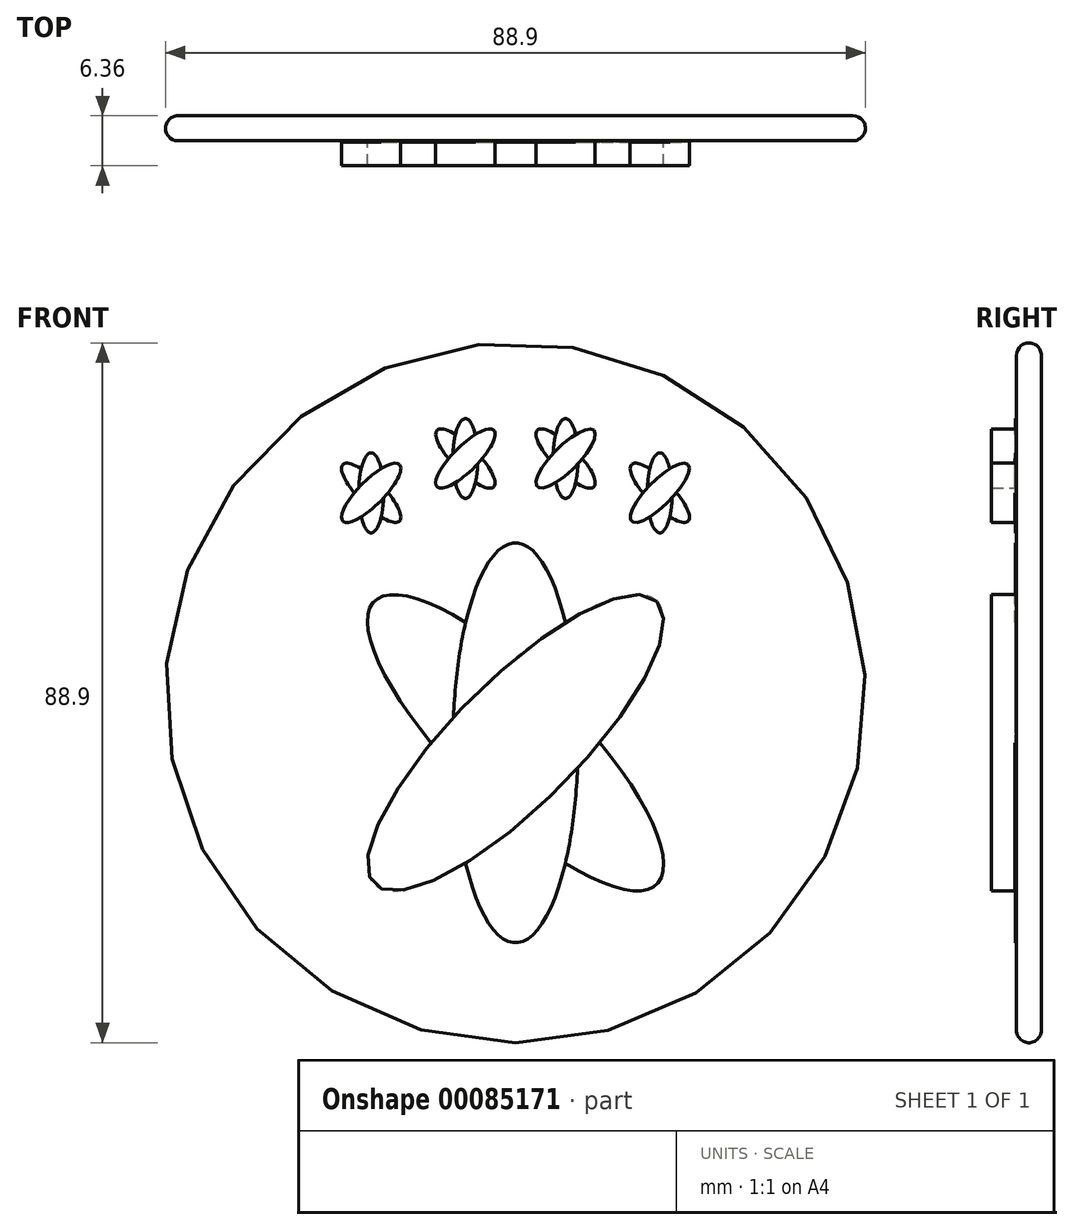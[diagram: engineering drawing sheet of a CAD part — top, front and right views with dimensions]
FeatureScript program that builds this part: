
annotation { "Feature Type Name" : "Feature", "Feature Type Description" : "" }
export const myFeature = defineFeature(function(context is Context, id is Id, definition is map)
    precondition{}
    {
        {
            var Q0;
            Q0=qCreatedBy(makeId("Front.planeOp"),FACE);
            var sketch = newSketch(context, id + "F0", { "sketchPlane" : qUnion([Q0])});
            skEllipse(sketch, "E0", {"center": v(0, 0) * mm, "majorRadius": 25.4 * mm, "minorRadius": 7.94 * mm, "majorAxis": v(0, 1)});
            skEllipse(sketch, "E1", {"center": v(0, 0) * mm, "majorRadius": 25.4 * mm, "minorRadius": 7.94 * mm, "majorAxis": v(0.7, 0.7)});
            skLineSegment(sketch, "E2", {"start": v(0, 0) * mm, "end": v(17.96, 17.96) * mm, "construction": true});
            skEllipse(sketch, "E3.MirrorC", {"center": v(0, 0) * mm, "majorRadius": 25.4 * mm, "minorRadius": 7.94 * mm, "majorAxis": v(-0.7, 0.7)});
            skLineSegment(sketch, "E4", {"start": v(0, 0) * mm, "end": v(-18.33, 31.75) * mm, "construction": true});
            skEllipse(sketch, "E5", {"center": v(-18.33, 31.75) * mm, "majorRadius": 5.08 * mm, "minorRadius": 1.59 * mm, "majorAxis": v(0, 1)});
            skEllipse(sketch, "E6", {"center": v(-18.33, 31.75) * mm, "majorRadius": 5.08 * mm, "minorRadius": 1.59 * mm, "majorAxis": v(0.7, 0.7)});
            skLineSegment(sketch, "E7", {"start": v(-18.33, 31.75) * mm, "end": v(-14.74, 35.34) * mm, "construction": true});
            skLineSegment(sketch, "E8", {"start": v(-18.33, 31.75) * mm, "end": v(-18.33, 36.83) * mm, "construction": true});
            skEllipse(sketch, "E9.MirrorC", {"center": v(-18.33, 31.75) * mm, "majorRadius": 5.08 * mm, "minorRadius": 1.59 * mm, "majorAxis": v(-0.7, 0.7)});
            skEllipse(sketch, "E10.MirrorC", {"center": v(18.33, 31.75) * mm, "majorRadius": 5.08 * mm, "minorRadius": 1.59 * mm, "majorAxis": v(0.7, 0.7)});
            skLineSegment(sketch, "E11.MirrorCS", {"start": v(18.33, 31.75) * mm, "end": v(18.33, 36.83) * mm, "construction": true});
            skLineSegment(sketch, "E12.MirrorCS", {"start": v(18.33, 31.75) * mm, "end": v(14.74, 35.34) * mm, "construction": true});
            skEllipse(sketch, "E13.MirrorC", {"center": v(18.33, 31.75) * mm, "majorRadius": 5.08 * mm, "minorRadius": 1.59 * mm, "majorAxis": v(-0.7, 0.7)});
            skEllipse(sketch, "E14.MirrorC", {"center": v(18.33, 31.75) * mm, "majorRadius": 5.08 * mm, "minorRadius": 1.59 * mm, "majorAxis": v(0, 1)});
            skCircle(sketch, "E15", {"center": v(0, 0) * mm, "radius": 36.66 * mm, "construction": true});
            skPoint(sketch, "E16.endSnap0", {"position": v(-5.61, 5.61) * mm});
            skLineSegment(sketch, "E17", {"start": v(0, 0) * mm, "end": v(-6.37, 36.1) * mm, "construction": true});
            skEllipse(sketch, "E18", {"center": v(-6.37, 36.1) * mm, "majorRadius": 5.08 * mm, "minorRadius": 1.59 * mm, "majorAxis": v(0, 1)});
            skEllipse(sketch, "E19", {"center": v(-6.37, 36.1) * mm, "majorRadius": 5.08 * mm, "minorRadius": 1.59 * mm, "majorAxis": v(0.7, 0.7)});
            skLineSegment(sketch, "E20", {"start": v(-6.37, 36.1) * mm, "end": v(-6.37, 41.18) * mm, "construction": true});
            skLineSegment(sketch, "E21", {"start": v(-6.37, 36.1) * mm, "end": v(-2.77, 39.7) * mm, "construction": true});
            skEllipse(sketch, "E22.MirrorC", {"center": v(-6.37, 36.1) * mm, "majorRadius": 5.08 * mm, "minorRadius": 1.59 * mm, "majorAxis": v(-0.7, 0.7)});
            skLineSegment(sketch, "E23.MirrorCS", {"start": v(6.37, 36.1) * mm, "end": v(6.37, 41.18) * mm, "construction": true});
            skLineSegment(sketch, "E24.MirrorCS", {"start": v(6.37, 36.1) * mm, "end": v(2.77, 39.7) * mm, "construction": true});
            skEllipse(sketch, "E25.MirrorC", {"center": v(6.37, 36.1) * mm, "majorRadius": 5.08 * mm, "minorRadius": 1.59 * mm, "majorAxis": v(0, 1)});
            skEllipse(sketch, "E26.MirrorC", {"center": v(6.37, 36.1) * mm, "majorRadius": 5.08 * mm, "minorRadius": 1.59 * mm, "majorAxis": v(0.7, 0.7)});
            skEllipse(sketch, "E27.MirrorC", {"center": v(6.37, 36.1) * mm, "majorRadius": 5.08 * mm, "minorRadius": 1.59 * mm, "majorAxis": v(-0.7, 0.7)});
            skSolve(sketch);
        }
        {
            var Q0;
            Q0=qCreatedBy(makeId("Front.planeOp"),FACE);
            var sketch = newSketch(context, id + "F5", { "sketchPlane" : qUnion([Q0])});
            skCircle(sketch, "E28", {"center": v(0, 6.35) * mm, "radius": 44.45 * mm});
            skSolve(sketch);
        }
        {
            var Q0;
            Q0 = qSketchRegion(id + "F5", true);
            extrude(context, id + "F6", {"entities" : qUnion([Q0]), "oppositeDirection" : true, "depth" : 3.17 * mm});
        }
        {
            var Q0;
            {var subQ0=sQuery(id+"F0.wireOp",EDGE,"E1");var subQ1=sQuery(id+"F0.wireOp",EDGE,"E0");var subQ2=makeQuery(id+"F0.imprint","INTERSECT",VERTEX,{"disambiguationData":[OD(1.0)],"derivedFrom":[subQ1,subQ0]});Q0=makeQuery(id+"F0.imprint","IMPRINT",FACE,{"disambiguationData":[TD([[makeQuery(id+"F0.imprint","IMPRINT",EDGE,{"disambiguationData":[TD([[subQ2,1.0]])],"derivedFrom":subQ1}),-1.0]])]});}
            var Q1;
            {var subQ0=sQuery(id+"F0.wireOp",EDGE,"E1");var subQ1=sQuery(id+"F0.wireOp",EDGE,"E0");var subQ2=makeQuery(id+"F0.imprint","INTERSECT",VERTEX,{"disambiguationData":[OD(1.0)],"derivedFrom":[subQ1,subQ0]});Q1=makeQuery(id+"F0.imprint","IMPRINT",FACE,{"disambiguationData":[TD([[makeQuery(id+"F0.imprint","IMPRINT",EDGE,{"disambiguationData":[TD([[subQ2,1.0]])],"derivedFrom":subQ1}),1.0]])]});}
            var Q2;
            {var subQ0=sQuery(id+"F0.wireOp",EDGE,"E1");var subQ1=sQuery(id+"F0.wireOp",EDGE,"E0");var subQ2=makeQuery(id+"F0.imprint","INTERSECT",VERTEX,{"disambiguationData":[OD(3.0)],"derivedFrom":[subQ1,subQ0]});Q2=makeQuery(id+"F0.imprint","IMPRINT",FACE,{"disambiguationData":[TD([[makeQuery(id+"F0.imprint","IMPRINT",EDGE,{"disambiguationData":[TD([[subQ2,-1.0]])],"derivedFrom":subQ1}),-1.0]])]});}
            var Q3;
            {var subQ0=sQuery(id+"F0.wireOp",EDGE,"E1");var subQ1=sQuery(id+"F0.wireOp",EDGE,"E0");var subQ6=makeQuery(id+"F0.imprint","INTERSECT",VERTEX,{"disambiguationData":[OD(2.0)],"derivedFrom":[subQ1,subQ0]});Q3=makeQuery(id+"F0.imprint","IMPRINT",FACE,{"disambiguationData":[TD([[makeQuery(id+"F0.imprint","IMPRINT",EDGE,{"disambiguationData":[TD([[subQ6,-1.0]])],"derivedFrom":subQ1}),1.0]])]});}
            var Q4;
            {var subQ0=sQuery(id+"F0.wireOp",EDGE,"E1");var subQ1=sQuery(id+"F0.wireOp",EDGE,"E0");var subQ2=makeQuery(id+"F0.imprint","INTERSECT",VERTEX,{"disambiguationData":[OD(2.0)],"derivedFrom":[subQ1,subQ0]});Q4=makeQuery(id+"F0.imprint","IMPRINT",FACE,{"disambiguationData":[TD([[makeQuery(id+"F0.imprint","IMPRINT",EDGE,{"disambiguationData":[TD([[subQ2,-1.0]])],"derivedFrom":subQ1}),-1.0]])]});}
            var Q5;
            {var subQ0=sQuery(id+"F0.wireOp",EDGE,"E1");var subQ1=sQuery(id+"F0.wireOp",EDGE,"E0");var subQ2=makeQuery(id+"F0.imprint","INTERSECT",VERTEX,{"disambiguationData":[OD(0.0)],"derivedFrom":[subQ1,subQ0]});Q5=makeQuery(id+"F0.imprint","IMPRINT",FACE,{"disambiguationData":[TD([[makeQuery(id+"F0.imprint","IMPRINT",EDGE,{"disambiguationData":[TD([[subQ2,1.0]])],"derivedFrom":subQ1}),1.0]])]});}
            var Q6;
            {var subQ0=sQuery(id+"F0.wireOp",EDGE,"E1");var subQ1=sQuery(id+"F0.wireOp",EDGE,"E0");var subQ2=makeQuery(id+"F0.imprint","INTERSECT",VERTEX,{"disambiguationData":[OD(0.0)],"derivedFrom":[subQ1,subQ0]});Q6=makeQuery(id+"F0.imprint","IMPRINT",FACE,{"disambiguationData":[TD([[makeQuery(id+"F0.imprint","IMPRINT",EDGE,{"disambiguationData":[TD([[subQ2,1.0]])],"derivedFrom":subQ1}),-1.0]])]});}
            var Q7;
            {var subQ0=sQuery(id+"F0.wireOp",EDGE,"E6");var subQ1=sQuery(id+"F0.wireOp",EDGE,"E5");var subQ2=makeQuery(id+"F0.imprint","INTERSECT",VERTEX,{"disambiguationData":[OD(1.0)],"derivedFrom":[subQ1,subQ0]});Q7=makeQuery(id+"F0.imprint","IMPRINT",FACE,{"disambiguationData":[TD([[makeQuery(id+"F0.imprint","IMPRINT",EDGE,{"disambiguationData":[TD([[subQ2,1.0]])],"derivedFrom":subQ1}),-1.0]])]});}
            var Q8;
            {var subQ0=sQuery(id+"F0.wireOp",EDGE,"E6");var subQ1=sQuery(id+"F0.wireOp",EDGE,"E5");var subQ2=makeQuery(id+"F0.imprint","INTERSECT",VERTEX,{"disambiguationData":[OD(1.0)],"derivedFrom":[subQ1,subQ0]});Q8=makeQuery(id+"F0.imprint","IMPRINT",FACE,{"disambiguationData":[TD([[makeQuery(id+"F0.imprint","IMPRINT",EDGE,{"disambiguationData":[TD([[subQ2,1.0]])],"derivedFrom":subQ1}),1.0]])]});}
            var Q9;
            {var subQ0=sQuery(id+"F0.wireOp",EDGE,"E6");var subQ1=sQuery(id+"F0.wireOp",EDGE,"E5");var subQ2=makeQuery(id+"F0.imprint","INTERSECT",VERTEX,{"disambiguationData":[OD(3.0)],"derivedFrom":[subQ1,subQ0]});Q9=makeQuery(id+"F0.imprint","IMPRINT",FACE,{"disambiguationData":[TD([[makeQuery(id+"F0.imprint","IMPRINT",EDGE,{"disambiguationData":[TD([[subQ2,-1.0]])],"derivedFrom":subQ1}),-1.0]])]});}
            var Q10;
            {var subQ0=sQuery(id+"F0.wireOp",EDGE,"E6");var subQ1=sQuery(id+"F0.wireOp",EDGE,"E5");var subQ5=makeQuery(id+"F0.imprint","INTERSECT",VERTEX,{"disambiguationData":[OD(2.0)],"derivedFrom":[subQ1,subQ0]});Q10=makeQuery(id+"F0.imprint","IMPRINT",FACE,{"disambiguationData":[TD([[makeQuery(id+"F0.imprint","IMPRINT",EDGE,{"disambiguationData":[TD([[subQ5,-1.0]])],"derivedFrom":subQ1}),1.0]])]});}
            var Q11;
            {var subQ0=sQuery(id+"F0.wireOp",EDGE,"E6");var subQ1=sQuery(id+"F0.wireOp",EDGE,"E5");var subQ2=makeQuery(id+"F0.imprint","INTERSECT",VERTEX,{"disambiguationData":[OD(2.0)],"derivedFrom":[subQ1,subQ0]});Q11=makeQuery(id+"F0.imprint","IMPRINT",FACE,{"disambiguationData":[TD([[makeQuery(id+"F0.imprint","IMPRINT",EDGE,{"disambiguationData":[TD([[subQ2,-1.0]])],"derivedFrom":subQ1}),-1.0]])]});}
            var Q12;
            {var subQ0=sQuery(id+"F0.wireOp",EDGE,"E6");var subQ1=sQuery(id+"F0.wireOp",EDGE,"E5");var subQ2=makeQuery(id+"F0.imprint","INTERSECT",VERTEX,{"disambiguationData":[OD(0.0)],"derivedFrom":[subQ1,subQ0]});Q12=makeQuery(id+"F0.imprint","IMPRINT",FACE,{"disambiguationData":[TD([[makeQuery(id+"F0.imprint","IMPRINT",EDGE,{"disambiguationData":[TD([[subQ2,1.0]])],"derivedFrom":subQ1}),1.0]])]});}
            var Q13;
            {var subQ0=sQuery(id+"F0.wireOp",EDGE,"E6");var subQ1=sQuery(id+"F0.wireOp",EDGE,"E5");var subQ2=makeQuery(id+"F0.imprint","INTERSECT",VERTEX,{"disambiguationData":[OD(0.0)],"derivedFrom":[subQ1,subQ0]});Q13=makeQuery(id+"F0.imprint","IMPRINT",FACE,{"disambiguationData":[TD([[makeQuery(id+"F0.imprint","IMPRINT",EDGE,{"disambiguationData":[TD([[subQ2,1.0]])],"derivedFrom":subQ1}),-1.0]])]});}
            var Q14;
            {var subQ0=sQuery(id+"F0.wireOp",EDGE,"E19");var subQ1=sQuery(id+"F0.wireOp",EDGE,"E18");var subQ2=makeQuery(id+"F0.imprint","INTERSECT",VERTEX,{"disambiguationData":[OD(0.0)],"derivedFrom":[subQ1,subQ0]});Q14=makeQuery(id+"F0.imprint","IMPRINT",FACE,{"disambiguationData":[TD([[makeQuery(id+"F0.imprint","IMPRINT",EDGE,{"disambiguationData":[TD([[subQ2,1.0]])],"derivedFrom":subQ1}),-1.0]])]});}
            var Q15;
            {var subQ0=sQuery(id+"F0.wireOp",EDGE,"E19");var subQ1=sQuery(id+"F0.wireOp",EDGE,"E18");var subQ2=makeQuery(id+"F0.imprint","INTERSECT",VERTEX,{"disambiguationData":[OD(0.0)],"derivedFrom":[subQ1,subQ0]});Q15=makeQuery(id+"F0.imprint","IMPRINT",FACE,{"disambiguationData":[TD([[makeQuery(id+"F0.imprint","IMPRINT",EDGE,{"disambiguationData":[TD([[subQ2,1.0]])],"derivedFrom":subQ1}),1.0]])]});}
            var Q16;
            {var subQ0=sQuery(id+"F0.wireOp",EDGE,"E19");var subQ1=sQuery(id+"F0.wireOp",EDGE,"E18");var subQ2=makeQuery(id+"F0.imprint","INTERSECT",VERTEX,{"disambiguationData":[OD(2.0)],"derivedFrom":[subQ1,subQ0]});Q16=makeQuery(id+"F0.imprint","IMPRINT",FACE,{"disambiguationData":[TD([[makeQuery(id+"F0.imprint","IMPRINT",EDGE,{"disambiguationData":[TD([[subQ2,-1.0]])],"derivedFrom":subQ1}),-1.0]])]});}
            var Q17;
            {var subQ0=sQuery(id+"F0.wireOp",EDGE,"E19");var subQ1=sQuery(id+"F0.wireOp",EDGE,"E18");var subQ5=makeQuery(id+"F0.imprint","INTERSECT",VERTEX,{"disambiguationData":[OD(2.0)],"derivedFrom":[subQ1,subQ0]});Q17=makeQuery(id+"F0.imprint","IMPRINT",FACE,{"disambiguationData":[TD([[makeQuery(id+"F0.imprint","IMPRINT",EDGE,{"disambiguationData":[TD([[subQ5,-1.0]])],"derivedFrom":subQ1}),1.0]])]});}
            var Q18;
            {var subQ0=sQuery(id+"F0.wireOp",EDGE,"E19");var subQ1=sQuery(id+"F0.wireOp",EDGE,"E18");var subQ2=makeQuery(id+"F0.imprint","INTERSECT",VERTEX,{"disambiguationData":[OD(3.0)],"derivedFrom":[subQ1,subQ0]});Q18=makeQuery(id+"F0.imprint","IMPRINT",FACE,{"disambiguationData":[TD([[makeQuery(id+"F0.imprint","IMPRINT",EDGE,{"disambiguationData":[TD([[subQ2,-1.0]])],"derivedFrom":subQ1}),-1.0]])]});}
            var Q19;
            {var subQ0=sQuery(id+"F0.wireOp",EDGE,"E19");var subQ1=sQuery(id+"F0.wireOp",EDGE,"E18");var subQ2=makeQuery(id+"F0.imprint","INTERSECT",VERTEX,{"disambiguationData":[OD(1.0)],"derivedFrom":[subQ1,subQ0]});Q19=makeQuery(id+"F0.imprint","IMPRINT",FACE,{"disambiguationData":[TD([[makeQuery(id+"F0.imprint","IMPRINT",EDGE,{"disambiguationData":[TD([[subQ2,1.0]])],"derivedFrom":subQ1}),-1.0]])]});}
            var Q20;
            {var subQ0=sQuery(id+"F0.wireOp",EDGE,"E19");var subQ1=sQuery(id+"F0.wireOp",EDGE,"E18");var subQ2=makeQuery(id+"F0.imprint","INTERSECT",VERTEX,{"disambiguationData":[OD(1.0)],"derivedFrom":[subQ1,subQ0]});Q20=makeQuery(id+"F0.imprint","IMPRINT",FACE,{"disambiguationData":[TD([[makeQuery(id+"F0.imprint","IMPRINT",EDGE,{"disambiguationData":[TD([[subQ2,1.0]])],"derivedFrom":subQ1}),1.0]])]});}
            var Q21;
            {var subQ0=sQuery(id+"F0.wireOp",EDGE,"E26.MirrorC");var subQ1=sQuery(id+"F0.wireOp",EDGE,"E25.MirrorC");var subQ2=makeQuery(id+"F0.imprint","INTERSECT",VERTEX,{"disambiguationData":[OD(0.0)],"derivedFrom":[subQ1,subQ0]});Q21=makeQuery(id+"F0.imprint","IMPRINT",FACE,{"disambiguationData":[TD([[makeQuery(id+"F0.imprint","IMPRINT",EDGE,{"disambiguationData":[TD([[subQ2,1.0]])],"derivedFrom":subQ1}),-1.0]])]});}
            var Q22;
            {var subQ0=sQuery(id+"F0.wireOp",EDGE,"E26.MirrorC");var subQ1=sQuery(id+"F0.wireOp",EDGE,"E25.MirrorC");var subQ2=makeQuery(id+"F0.imprint","INTERSECT",VERTEX,{"disambiguationData":[OD(0.0)],"derivedFrom":[subQ1,subQ0]});Q22=makeQuery(id+"F0.imprint","IMPRINT",FACE,{"disambiguationData":[TD([[makeQuery(id+"F0.imprint","IMPRINT",EDGE,{"disambiguationData":[TD([[subQ2,1.0]])],"derivedFrom":subQ1}),1.0]])]});}
            var Q23;
            {var subQ0=sQuery(id+"F0.wireOp",EDGE,"E26.MirrorC");var subQ1=sQuery(id+"F0.wireOp",EDGE,"E25.MirrorC");var subQ2=makeQuery(id+"F0.imprint","INTERSECT",VERTEX,{"disambiguationData":[OD(2.0)],"derivedFrom":[subQ1,subQ0]});Q23=makeQuery(id+"F0.imprint","IMPRINT",FACE,{"disambiguationData":[TD([[makeQuery(id+"F0.imprint","IMPRINT",EDGE,{"disambiguationData":[TD([[subQ2,-1.0]])],"derivedFrom":subQ1}),-1.0]])]});}
            var Q24;
            {var subQ0=sQuery(id+"F0.wireOp",EDGE,"E26.MirrorC");var subQ1=sQuery(id+"F0.wireOp",EDGE,"E25.MirrorC");var subQ5=makeQuery(id+"F0.imprint","INTERSECT",VERTEX,{"disambiguationData":[OD(2.0)],"derivedFrom":[subQ1,subQ0]});Q24=makeQuery(id+"F0.imprint","IMPRINT",FACE,{"disambiguationData":[TD([[makeQuery(id+"F0.imprint","IMPRINT",EDGE,{"disambiguationData":[TD([[subQ5,-1.0]])],"derivedFrom":subQ1}),1.0]])]});}
            var Q25;
            {var subQ0=sQuery(id+"F0.wireOp",EDGE,"E26.MirrorC");var subQ1=sQuery(id+"F0.wireOp",EDGE,"E25.MirrorC");var subQ2=makeQuery(id+"F0.imprint","INTERSECT",VERTEX,{"disambiguationData":[OD(3.0)],"derivedFrom":[subQ1,subQ0]});Q25=makeQuery(id+"F0.imprint","IMPRINT",FACE,{"disambiguationData":[TD([[makeQuery(id+"F0.imprint","IMPRINT",EDGE,{"disambiguationData":[TD([[subQ2,-1.0]])],"derivedFrom":subQ1}),-1.0]])]});}
            var Q26;
            {var subQ0=sQuery(id+"F0.wireOp",EDGE,"E26.MirrorC");var subQ1=sQuery(id+"F0.wireOp",EDGE,"E25.MirrorC");var subQ2=makeQuery(id+"F0.imprint","INTERSECT",VERTEX,{"disambiguationData":[OD(1.0)],"derivedFrom":[subQ1,subQ0]});Q26=makeQuery(id+"F0.imprint","IMPRINT",FACE,{"disambiguationData":[TD([[makeQuery(id+"F0.imprint","IMPRINT",EDGE,{"disambiguationData":[TD([[subQ2,1.0]])],"derivedFrom":subQ1}),1.0]])]});}
            var Q27;
            {var subQ0=sQuery(id+"F0.wireOp",EDGE,"E26.MirrorC");var subQ1=sQuery(id+"F0.wireOp",EDGE,"E25.MirrorC");var subQ2=makeQuery(id+"F0.imprint","INTERSECT",VERTEX,{"disambiguationData":[OD(1.0)],"derivedFrom":[subQ1,subQ0]});Q27=makeQuery(id+"F0.imprint","IMPRINT",FACE,{"disambiguationData":[TD([[makeQuery(id+"F0.imprint","IMPRINT",EDGE,{"disambiguationData":[TD([[subQ2,1.0]])],"derivedFrom":subQ1}),-1.0]])]});}
            var Q28;
            {var subQ0=sQuery(id+"F0.wireOp",EDGE,"E13.MirrorC");var subQ1=sQuery(id+"F0.wireOp",EDGE,"E10.MirrorC");var subQ2=makeQuery(id+"F0.imprint","INTERSECT",VERTEX,{"disambiguationData":[OD(0.0)],"derivedFrom":[subQ1,subQ0]});Q28=makeQuery(id+"F0.imprint","IMPRINT",FACE,{"disambiguationData":[TD([[makeQuery(id+"F0.imprint","IMPRINT",EDGE,{"disambiguationData":[TD([[subQ2,-1.0]])],"derivedFrom":subQ1}),1.0]])]});}
            var Q29;
            {var subQ0=sQuery(id+"F0.wireOp",EDGE,"E14.MirrorC");var subQ1=sQuery(id+"F0.wireOp",EDGE,"E10.MirrorC");var subQ2=makeQuery(id+"F0.imprint","INTERSECT",VERTEX,{"disambiguationData":[OD(1.0)],"derivedFrom":[subQ1,subQ0]});Q29=makeQuery(id+"F0.imprint","IMPRINT",FACE,{"disambiguationData":[TD([[makeQuery(id+"F0.imprint","IMPRINT",EDGE,{"disambiguationData":[TD([[subQ2,-1.0]])],"derivedFrom":subQ1}),1.0]])]});}
            var Q30;
            {var subQ0=sQuery(id+"F0.wireOp",EDGE,"E13.MirrorC");var subQ1=sQuery(id+"F0.wireOp",EDGE,"E10.MirrorC");var subQ2=makeQuery(id+"F0.imprint","INTERSECT",VERTEX,{"disambiguationData":[OD(0.0)],"derivedFrom":[subQ1,subQ0]});Q30=makeQuery(id+"F0.imprint","IMPRINT",FACE,{"disambiguationData":[TD([[makeQuery(id+"F0.imprint","IMPRINT",EDGE,{"disambiguationData":[TD([[subQ2,1.0]])],"derivedFrom":subQ1}),1.0]])]});}
            var Q31;
            {var subQ0=sQuery(id+"F0.wireOp",EDGE,"E13.MirrorC");var subQ1=sQuery(id+"F0.wireOp",EDGE,"E10.MirrorC");var subQ2=makeQuery(id+"F0.imprint","INTERSECT",VERTEX,{"disambiguationData":[OD(2.0)],"derivedFrom":[subQ1,subQ0]});Q31=makeQuery(id+"F0.imprint","IMPRINT",FACE,{"disambiguationData":[TD([[makeQuery(id+"F0.imprint","IMPRINT",EDGE,{"disambiguationData":[TD([[subQ2,-1.0]])],"derivedFrom":subQ1}),1.0]])]});}
            var Q32;
            {var subQ0=sQuery(id+"F0.wireOp",EDGE,"E14.MirrorC");var subQ1=sQuery(id+"F0.wireOp",EDGE,"E10.MirrorC");var subQ2=makeQuery(id+"F0.imprint","INTERSECT",VERTEX,{"disambiguationData":[OD(0.0)],"derivedFrom":[subQ1,subQ0]});Q32=makeQuery(id+"F0.imprint","IMPRINT",FACE,{"disambiguationData":[TD([[makeQuery(id+"F0.imprint","IMPRINT",EDGE,{"disambiguationData":[TD([[subQ2,-1.0]])],"derivedFrom":subQ1}),1.0]])]});}
            var Q33;
            {var subQ0=sQuery(id+"F0.wireOp",EDGE,"E13.MirrorC");var subQ1=sQuery(id+"F0.wireOp",EDGE,"E10.MirrorC");var subQ2=makeQuery(id+"F0.imprint","INTERSECT",VERTEX,{"disambiguationData":[OD(1.0)],"derivedFrom":[subQ1,subQ0]});Q33=makeQuery(id+"F0.imprint","IMPRINT",FACE,{"disambiguationData":[TD([[makeQuery(id+"F0.imprint","IMPRINT",EDGE,{"disambiguationData":[TD([[subQ2,1.0]])],"derivedFrom":subQ1}),1.0]])]});}
            var Q34;
            {var subQ0=sQuery(id+"F0.wireOp",EDGE,"E14.MirrorC");var subQ1=sQuery(id+"F0.wireOp",EDGE,"E10.MirrorC");var subQ2=makeQuery(id+"F0.imprint","INTERSECT",VERTEX,{"disambiguationData":[OD(0.0)],"derivedFrom":[subQ1,subQ0]});Q34=makeQuery(id+"F0.imprint","IMPRINT",FACE,{"disambiguationData":[TD([[makeQuery(id+"F0.imprint","IMPRINT",EDGE,{"disambiguationData":[TD([[subQ2,1.0]])],"derivedFrom":subQ1}),1.0]])]});}
            extrude(context, id + "F1", {"entities" : qUnion([Q0, Q1, Q2, Q3, Q4, Q5, Q6, Q7, Q8, Q9, Q10, Q11, Q12, Q13, Q14, Q15, Q16, Q17, Q18, Q19, Q20, Q21, Q22, Q23, Q24, Q25, Q26, Q27, Q28, Q29, Q30, Q31, Q32, Q33, Q34]), "operationType" : NewBodyOperationType.ADD, "depth" : 3.17 * mm});
        }
        {
            var Q0;
            {var subQ0=sQuery(id+"F0.wireOp",EDGE,"E3.MirrorC");var subQ1=sQuery(id+"F0.wireOp",EDGE,"E0");var subQ2=makeQuery(id+"F0.imprint","INTERSECT",VERTEX,{"disambiguationData":[OD(0.0)],"derivedFrom":[subQ1,subQ0]});Q0=makeQuery(id+"F0.imprint","IMPRINT",FACE,{"disambiguationData":[TD([[makeQuery(id+"F0.imprint","IMPRINT",EDGE,{"disambiguationData":[TD([[subQ2,1.0]])],"derivedFrom":subQ1}),1.0]])]});}
            var Q1;
            {var subQ0=sQuery(id+"F0.wireOp",EDGE,"E3.MirrorC");var subQ1=sQuery(id+"F0.wireOp",EDGE,"E0");var subQ2=makeQuery(id+"F0.imprint","INTERSECT",VERTEX,{"disambiguationData":[OD(0.0)],"derivedFrom":[subQ1,subQ0]});Q1=makeQuery(id+"F0.imprint","IMPRINT",FACE,{"disambiguationData":[TD([[makeQuery(id+"F0.imprint","IMPRINT",EDGE,{"disambiguationData":[TD([[subQ2,-1.0]])],"derivedFrom":subQ1}),1.0]])]});}
            var Q2;
            {var subQ0=sQuery(id+"F0.wireOp",EDGE,"E3.MirrorC");var subQ1=sQuery(id+"F0.wireOp",EDGE,"E0");var subQ2=makeQuery(id+"F0.imprint","INTERSECT",VERTEX,{"disambiguationData":[OD(1.0)],"derivedFrom":[subQ1,subQ0]});Q2=makeQuery(id+"F0.imprint","IMPRINT",FACE,{"disambiguationData":[TD([[makeQuery(id+"F0.imprint","IMPRINT",EDGE,{"disambiguationData":[TD([[subQ2,-1.0]])],"derivedFrom":subQ1}),1.0]])]});}
            var Q3;
            {var subQ0=sQuery(id+"F0.wireOp",EDGE,"E1");var subQ1=sQuery(id+"F0.wireOp",EDGE,"E0");var subQ2=makeQuery(id+"F0.imprint","INTERSECT",VERTEX,{"disambiguationData":[OD(0.0)],"derivedFrom":[subQ1,subQ0]});Q3=makeQuery(id+"F0.imprint","IMPRINT",FACE,{"disambiguationData":[TD([[makeQuery(id+"F0.imprint","IMPRINT",EDGE,{"disambiguationData":[TD([[subQ2,-1.0]])],"derivedFrom":subQ1}),1.0]])]});}
            var Q4;
            {var subQ0=sQuery(id+"F0.wireOp",EDGE,"E6");var subQ1=sQuery(id+"F0.wireOp",EDGE,"E5");var subQ2=makeQuery(id+"F0.imprint","INTERSECT",VERTEX,{"disambiguationData":[OD(0.0)],"derivedFrom":[subQ1,subQ0]});Q4=makeQuery(id+"F0.imprint","IMPRINT",FACE,{"disambiguationData":[TD([[makeQuery(id+"F0.imprint","IMPRINT",EDGE,{"disambiguationData":[TD([[subQ2,-1.0]])],"derivedFrom":subQ1}),1.0]])]});}
            var Q5;
            {var subQ0=sQuery(id+"F0.wireOp",EDGE,"E9.MirrorC");var subQ1=sQuery(id+"F0.wireOp",EDGE,"E5");var subQ2=makeQuery(id+"F0.imprint","INTERSECT",VERTEX,{"disambiguationData":[OD(1.0)],"derivedFrom":[subQ1,subQ0]});Q5=makeQuery(id+"F0.imprint","IMPRINT",FACE,{"disambiguationData":[TD([[makeQuery(id+"F0.imprint","IMPRINT",EDGE,{"disambiguationData":[TD([[subQ2,-1.0]])],"derivedFrom":subQ1}),1.0]])]});}
            var Q6;
            {var subQ0=sQuery(id+"F0.wireOp",EDGE,"E9.MirrorC");var subQ1=sQuery(id+"F0.wireOp",EDGE,"E5");var subQ2=makeQuery(id+"F0.imprint","INTERSECT",VERTEX,{"disambiguationData":[OD(0.0)],"derivedFrom":[subQ1,subQ0]});Q6=makeQuery(id+"F0.imprint","IMPRINT",FACE,{"disambiguationData":[TD([[makeQuery(id+"F0.imprint","IMPRINT",EDGE,{"disambiguationData":[TD([[subQ2,-1.0]])],"derivedFrom":subQ1}),1.0]])]});}
            var Q7;
            {var subQ0=sQuery(id+"F0.wireOp",EDGE,"E9.MirrorC");var subQ1=sQuery(id+"F0.wireOp",EDGE,"E5");var subQ2=makeQuery(id+"F0.imprint","INTERSECT",VERTEX,{"disambiguationData":[OD(0.0)],"derivedFrom":[subQ1,subQ0]});Q7=makeQuery(id+"F0.imprint","IMPRINT",FACE,{"disambiguationData":[TD([[makeQuery(id+"F0.imprint","IMPRINT",EDGE,{"disambiguationData":[TD([[subQ2,1.0]])],"derivedFrom":subQ1}),1.0]])]});}
            var Q8;
            {var subQ0=sQuery(id+"F0.wireOp",EDGE,"E22.MirrorC");var subQ1=sQuery(id+"F0.wireOp",EDGE,"E18");var subQ2=makeQuery(id+"F0.imprint","INTERSECT",VERTEX,{"disambiguationData":[OD(0.0)],"derivedFrom":[subQ1,subQ0]});Q8=makeQuery(id+"F0.imprint","IMPRINT",FACE,{"disambiguationData":[TD([[makeQuery(id+"F0.imprint","IMPRINT",EDGE,{"disambiguationData":[TD([[subQ2,-1.0]])],"derivedFrom":subQ1}),1.0]])]});}
            var Q9;
            {var subQ0=sQuery(id+"F0.wireOp",EDGE,"E22.MirrorC");var subQ1=sQuery(id+"F0.wireOp",EDGE,"E18");var subQ2=makeQuery(id+"F0.imprint","INTERSECT",VERTEX,{"disambiguationData":[OD(0.0)],"derivedFrom":[subQ1,subQ0]});Q9=makeQuery(id+"F0.imprint","IMPRINT",FACE,{"disambiguationData":[TD([[makeQuery(id+"F0.imprint","IMPRINT",EDGE,{"disambiguationData":[TD([[subQ2,1.0]])],"derivedFrom":subQ1}),1.0]])]});}
            var Q10;
            {var subQ0=sQuery(id+"F0.wireOp",EDGE,"E22.MirrorC");var subQ1=sQuery(id+"F0.wireOp",EDGE,"E18");var subQ2=makeQuery(id+"F0.imprint","INTERSECT",VERTEX,{"disambiguationData":[OD(1.0)],"derivedFrom":[subQ1,subQ0]});Q10=makeQuery(id+"F0.imprint","IMPRINT",FACE,{"disambiguationData":[TD([[makeQuery(id+"F0.imprint","IMPRINT",EDGE,{"disambiguationData":[TD([[subQ2,-1.0]])],"derivedFrom":subQ1}),1.0]])]});}
            var Q11;
            {var subQ0=sQuery(id+"F0.wireOp",EDGE,"E19");var subQ1=sQuery(id+"F0.wireOp",EDGE,"E18");var subQ2=makeQuery(id+"F0.imprint","INTERSECT",VERTEX,{"disambiguationData":[OD(0.0)],"derivedFrom":[subQ1,subQ0]});Q11=makeQuery(id+"F0.imprint","IMPRINT",FACE,{"disambiguationData":[TD([[makeQuery(id+"F0.imprint","IMPRINT",EDGE,{"disambiguationData":[TD([[subQ2,-1.0]])],"derivedFrom":subQ1}),1.0]])]});}
            var Q12;
            {var subQ0=sQuery(id+"F0.wireOp",EDGE,"E26.MirrorC");var subQ1=sQuery(id+"F0.wireOp",EDGE,"E25.MirrorC");var subQ2=makeQuery(id+"F0.imprint","INTERSECT",VERTEX,{"disambiguationData":[OD(0.0)],"derivedFrom":[subQ1,subQ0]});Q12=makeQuery(id+"F0.imprint","IMPRINT",FACE,{"disambiguationData":[TD([[makeQuery(id+"F0.imprint","IMPRINT",EDGE,{"disambiguationData":[TD([[subQ2,-1.0]])],"derivedFrom":subQ1}),1.0]])]});}
            var Q13;
            {var subQ0=sQuery(id+"F0.wireOp",EDGE,"E27.MirrorC");var subQ1=sQuery(id+"F0.wireOp",EDGE,"E25.MirrorC");var subQ2=makeQuery(id+"F0.imprint","INTERSECT",VERTEX,{"disambiguationData":[OD(1.0)],"derivedFrom":[subQ1,subQ0]});Q13=makeQuery(id+"F0.imprint","IMPRINT",FACE,{"disambiguationData":[TD([[makeQuery(id+"F0.imprint","IMPRINT",EDGE,{"disambiguationData":[TD([[subQ2,-1.0]])],"derivedFrom":subQ1}),1.0]])]});}
            var Q14;
            {var subQ0=sQuery(id+"F0.wireOp",EDGE,"E27.MirrorC");var subQ1=sQuery(id+"F0.wireOp",EDGE,"E25.MirrorC");var subQ2=makeQuery(id+"F0.imprint","INTERSECT",VERTEX,{"disambiguationData":[OD(0.0)],"derivedFrom":[subQ1,subQ0]});Q14=makeQuery(id+"F0.imprint","IMPRINT",FACE,{"disambiguationData":[TD([[makeQuery(id+"F0.imprint","IMPRINT",EDGE,{"disambiguationData":[TD([[subQ2,-1.0]])],"derivedFrom":subQ1}),1.0]])]});}
            var Q15;
            {var subQ0=sQuery(id+"F0.wireOp",EDGE,"E27.MirrorC");var subQ1=sQuery(id+"F0.wireOp",EDGE,"E25.MirrorC");var subQ2=makeQuery(id+"F0.imprint","INTERSECT",VERTEX,{"disambiguationData":[OD(0.0)],"derivedFrom":[subQ1,subQ0]});Q15=makeQuery(id+"F0.imprint","IMPRINT",FACE,{"disambiguationData":[TD([[makeQuery(id+"F0.imprint","IMPRINT",EDGE,{"disambiguationData":[TD([[subQ2,1.0]])],"derivedFrom":subQ1}),1.0]])]});}
            var Q16;
            {var subQ0=sQuery(id+"F0.wireOp",EDGE,"E14.MirrorC");var subQ1=sQuery(id+"F0.wireOp",EDGE,"E10.MirrorC");var subQ2=makeQuery(id+"F0.imprint","INTERSECT",VERTEX,{"disambiguationData":[OD(0.0)],"derivedFrom":[subQ1,subQ0]});Q16=makeQuery(id+"F0.imprint","IMPRINT",FACE,{"disambiguationData":[TD([[makeQuery(id+"F0.imprint","IMPRINT",EDGE,{"disambiguationData":[TD([[subQ2,-1.0]])],"derivedFrom":subQ1}),-1.0]])]});}
            var Q17;
            {var subQ0=sQuery(id+"F0.wireOp",EDGE,"E13.MirrorC");var subQ1=sQuery(id+"F0.wireOp",EDGE,"E10.MirrorC");var subQ2=makeQuery(id+"F0.imprint","INTERSECT",VERTEX,{"disambiguationData":[OD(2.0)],"derivedFrom":[subQ1,subQ0]});Q17=makeQuery(id+"F0.imprint","IMPRINT",FACE,{"disambiguationData":[TD([[makeQuery(id+"F0.imprint","IMPRINT",EDGE,{"disambiguationData":[TD([[subQ2,-1.0]])],"derivedFrom":subQ1}),-1.0]])]});}
            var Q18;
            {var subQ0=sQuery(id+"F0.wireOp",EDGE,"E13.MirrorC");var subQ1=sQuery(id+"F0.wireOp",EDGE,"E10.MirrorC");var subQ2=makeQuery(id+"F0.imprint","INTERSECT",VERTEX,{"disambiguationData":[OD(3.0)],"derivedFrom":[subQ1,subQ0]});Q18=makeQuery(id+"F0.imprint","IMPRINT",FACE,{"disambiguationData":[TD([[makeQuery(id+"F0.imprint","IMPRINT",EDGE,{"disambiguationData":[TD([[subQ2,-1.0]])],"derivedFrom":subQ1}),-1.0]])]});}
            var Q19;
            {var subQ0=sQuery(id+"F0.wireOp",EDGE,"E14.MirrorC");var subQ1=sQuery(id+"F0.wireOp",EDGE,"E10.MirrorC");var subQ2=makeQuery(id+"F0.imprint","INTERSECT",VERTEX,{"disambiguationData":[OD(1.0)],"derivedFrom":[subQ1,subQ0]});Q19=makeQuery(id+"F0.imprint","IMPRINT",FACE,{"disambiguationData":[TD([[makeQuery(id+"F0.imprint","IMPRINT",EDGE,{"disambiguationData":[TD([[subQ2,-1.0]])],"derivedFrom":subQ1}),-1.0]])]});}
            extrude(context, id + "F2", {"entities" : qUnion([Q0, Q1, Q2, Q3, Q4, Q5, Q6, Q7, Q8, Q9, Q10, Q11, Q12, Q13, Q14, Q15, Q16, Q17, Q18, Q19]), "operationType" : NewBodyOperationType.ADD, "depth" : (.125 + (1 / 32)) * mm});
        }
        {
            var Q0;
            {var subQ0=sQuery(id+"F0.wireOp",EDGE,"E3.MirrorC");var subQ1=sQuery(id+"F0.wireOp",EDGE,"E0");var subQ2=makeQuery(id+"F0.imprint","INTERSECT",VERTEX,{"disambiguationData":[OD(0.0)],"derivedFrom":[subQ1,subQ0]});Q0=makeQuery(id+"F0.imprint","IMPRINT",FACE,{"disambiguationData":[TD([[makeQuery(id+"F0.imprint","IMPRINT",EDGE,{"disambiguationData":[TD([[subQ2,-1.0]])],"derivedFrom":subQ1}),-1.0]])]});}
            var Q1;
            {var subQ0=sQuery(id+"F0.wireOp",EDGE,"E3.MirrorC");var subQ1=sQuery(id+"F0.wireOp",EDGE,"E0");var subQ2=makeQuery(id+"F0.imprint","INTERSECT",VERTEX,{"disambiguationData":[OD(1.0)],"derivedFrom":[subQ1,subQ0]});Q1=makeQuery(id+"F0.imprint","IMPRINT",FACE,{"disambiguationData":[TD([[makeQuery(id+"F0.imprint","IMPRINT",EDGE,{"disambiguationData":[TD([[subQ2,-1.0]])],"derivedFrom":subQ1}),-1.0]])]});}
            var Q2;
            {var subQ0=sQuery(id+"F0.wireOp",EDGE,"E9.MirrorC");var subQ1=sQuery(id+"F0.wireOp",EDGE,"E5");var subQ2=makeQuery(id+"F0.imprint","INTERSECT",VERTEX,{"disambiguationData":[OD(0.0)],"derivedFrom":[subQ1,subQ0]});Q2=makeQuery(id+"F0.imprint","IMPRINT",FACE,{"disambiguationData":[TD([[makeQuery(id+"F0.imprint","IMPRINT",EDGE,{"disambiguationData":[TD([[subQ2,-1.0]])],"derivedFrom":subQ1}),-1.0]])]});}
            var Q3;
            {var subQ0=sQuery(id+"F0.wireOp",EDGE,"E9.MirrorC");var subQ1=sQuery(id+"F0.wireOp",EDGE,"E5");var subQ2=makeQuery(id+"F0.imprint","INTERSECT",VERTEX,{"disambiguationData":[OD(1.0)],"derivedFrom":[subQ1,subQ0]});Q3=makeQuery(id+"F0.imprint","IMPRINT",FACE,{"disambiguationData":[TD([[makeQuery(id+"F0.imprint","IMPRINT",EDGE,{"disambiguationData":[TD([[subQ2,-1.0]])],"derivedFrom":subQ1}),-1.0]])]});}
            var Q4;
            {var subQ0=sQuery(id+"F0.wireOp",EDGE,"E22.MirrorC");var subQ1=sQuery(id+"F0.wireOp",EDGE,"E18");var subQ2=makeQuery(id+"F0.imprint","INTERSECT",VERTEX,{"disambiguationData":[OD(0.0)],"derivedFrom":[subQ1,subQ0]});Q4=makeQuery(id+"F0.imprint","IMPRINT",FACE,{"disambiguationData":[TD([[makeQuery(id+"F0.imprint","IMPRINT",EDGE,{"disambiguationData":[TD([[subQ2,-1.0]])],"derivedFrom":subQ1}),-1.0]])]});}
            var Q5;
            {var subQ0=sQuery(id+"F0.wireOp",EDGE,"E22.MirrorC");var subQ1=sQuery(id+"F0.wireOp",EDGE,"E18");var subQ2=makeQuery(id+"F0.imprint","INTERSECT",VERTEX,{"disambiguationData":[OD(1.0)],"derivedFrom":[subQ1,subQ0]});Q5=makeQuery(id+"F0.imprint","IMPRINT",FACE,{"disambiguationData":[TD([[makeQuery(id+"F0.imprint","IMPRINT",EDGE,{"disambiguationData":[TD([[subQ2,-1.0]])],"derivedFrom":subQ1}),-1.0]])]});}
            var Q6;
            {var subQ0=sQuery(id+"F0.wireOp",EDGE,"E27.MirrorC");var subQ1=sQuery(id+"F0.wireOp",EDGE,"E25.MirrorC");var subQ2=makeQuery(id+"F0.imprint","INTERSECT",VERTEX,{"disambiguationData":[OD(0.0)],"derivedFrom":[subQ1,subQ0]});Q6=makeQuery(id+"F0.imprint","IMPRINT",FACE,{"disambiguationData":[TD([[makeQuery(id+"F0.imprint","IMPRINT",EDGE,{"disambiguationData":[TD([[subQ2,-1.0]])],"derivedFrom":subQ1}),-1.0]])]});}
            var Q7;
            {var subQ0=sQuery(id+"F0.wireOp",EDGE,"E27.MirrorC");var subQ1=sQuery(id+"F0.wireOp",EDGE,"E25.MirrorC");var subQ2=makeQuery(id+"F0.imprint","INTERSECT",VERTEX,{"disambiguationData":[OD(1.0)],"derivedFrom":[subQ1,subQ0]});Q7=makeQuery(id+"F0.imprint","IMPRINT",FACE,{"disambiguationData":[TD([[makeQuery(id+"F0.imprint","IMPRINT",EDGE,{"disambiguationData":[TD([[subQ2,-1.0]])],"derivedFrom":subQ1}),-1.0]])]});}
            var Q8;
            {var subQ0=sQuery(id+"F0.wireOp",EDGE,"E13.MirrorC");var subQ1=sQuery(id+"F0.wireOp",EDGE,"E10.MirrorC");var subQ2=makeQuery(id+"F0.imprint","INTERSECT",VERTEX,{"disambiguationData":[OD(0.0)],"derivedFrom":[subQ1,subQ0]});Q8=makeQuery(id+"F0.imprint","IMPRINT",FACE,{"disambiguationData":[TD([[makeQuery(id+"F0.imprint","IMPRINT",EDGE,{"disambiguationData":[TD([[subQ2,1.0]])],"derivedFrom":subQ1}),-1.0]])]});}
            var Q9;
            {var subQ0=sQuery(id+"F0.wireOp",EDGE,"E13.MirrorC");var subQ1=sQuery(id+"F0.wireOp",EDGE,"E10.MirrorC");var subQ2=makeQuery(id+"F0.imprint","INTERSECT",VERTEX,{"disambiguationData":[OD(1.0)],"derivedFrom":[subQ1,subQ0]});Q9=makeQuery(id+"F0.imprint","IMPRINT",FACE,{"disambiguationData":[TD([[makeQuery(id+"F0.imprint","IMPRINT",EDGE,{"disambiguationData":[TD([[subQ2,1.0]])],"derivedFrom":subQ1}),-1.0]])]});}
            extrude(context, id + "F3", {"entities" : qUnion([Q0, Q1, Q2, Q3, Q4, Q5, Q6, Q7, Q8, Q9]), "operationType" : NewBodyOperationType.ADD, "depth" : (.125 + (1 / 16)) * mm});
        }
        {
            var Q0;
            Q0=makeQuery(id+"F6.opExtrude","CAP_EDGE",EDGE,{"disambiguationData":[OSD([sQuery(id+"F5.wireOp",EDGE,"E28")])],"isStart":true});
            var Q1;
            Q1=makeQuery(id+"F6.opExtrude","CAP_EDGE",EDGE,{"disambiguationData":[OSD([sQuery(id+"F5.wireOp",EDGE,"E28")])],"isStart":false});
            fillet(context, id + "F4", {"entities" : qUnion([Q0, Q1]), "radius" : 1.59 * mm, "tangentPropagation" : true, "allowEdgeOverflow" : false});
        }
    });
